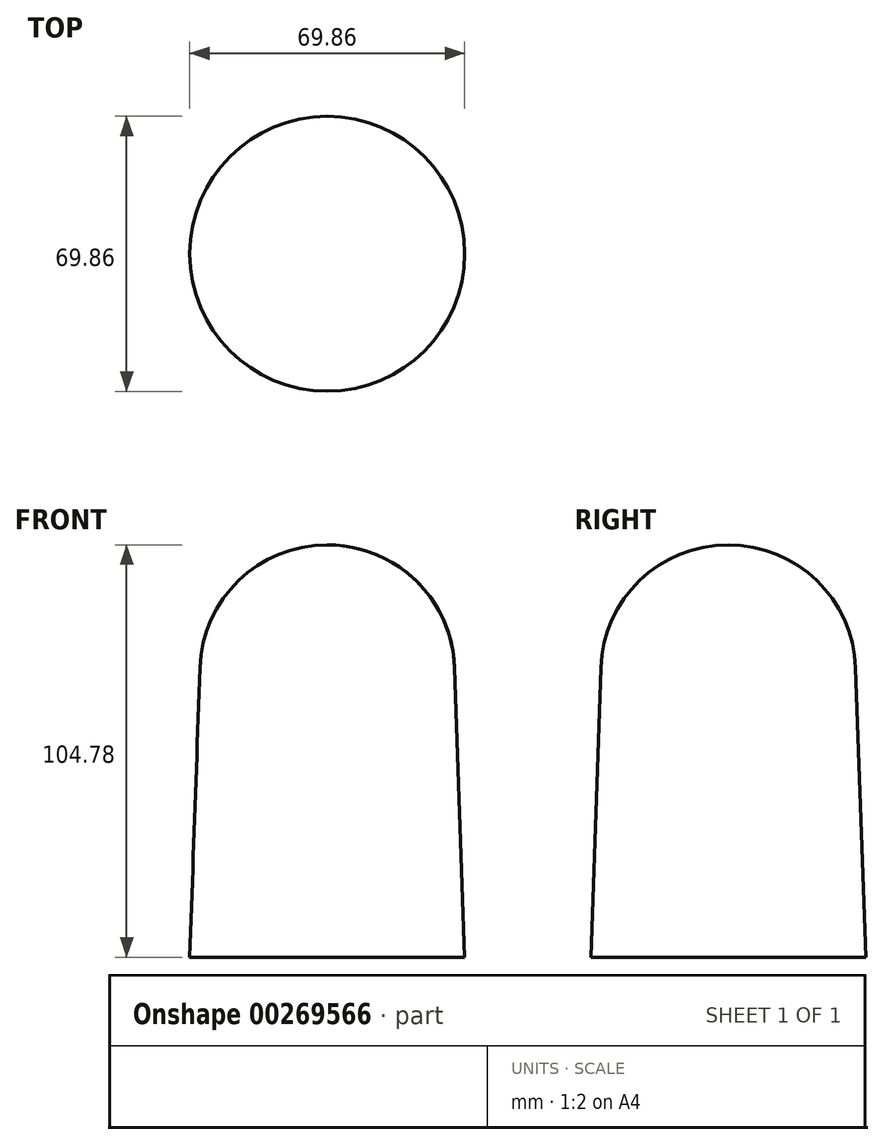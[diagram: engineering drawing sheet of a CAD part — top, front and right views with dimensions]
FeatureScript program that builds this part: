
annotation { "Feature Type Name" : "Feature", "Feature Type Description" : "" }
export const myFeature = defineFeature(function(context is Context, id is Id, definition is map)
    precondition{}
    {
        {
            var Q0;
            Q0=qCreatedBy(makeId("Front.planeOp"),FACE);
            var sketch = newSketch(context, id + "F1", { "sketchPlane" : qUnion([Q0])});
            skLineSegment(sketch, "E0", {"start": v(0, 0) * mm, "end": v(0, 104.78) * mm});
            skLineSegment(sketch, "E1", {"start": v(0, 0) * mm, "end": v(-34.93, 0) * mm});
            skLineSegment(sketch, "E2", {"start": v(-34.93, 0) * mm, "end": v(-32.36, 73.53) * mm});
            skArc(sketch, "E3", {"start": v(-32.36, 73.53) * mm, "mid": v(-22.5, 95.69) * mm, "end": v(0, 104.78) * mm});
            skSolve(sketch);
        }
        {
            var Q0;
            Q0=makeQuery(id+"F1.imprint","IMPRINT",FACE,{"disambiguationData":[TD([[makeQuery(id+"F1.imprint","IMPRINT",EDGE,{"derivedFrom":sQuery(id+"F1.wireOp",EDGE,"E0")}),1.0]])]});
            var Q1;
            Q1=sQuery(id+"F1.wireOp",EDGE,"E0");
            revolve(context, id + "F0", {"entities" : qUnion([Q0]), "axis" : qUnion([Q1]), "revolveType" : RevolveType.FULL});
        }
    });
